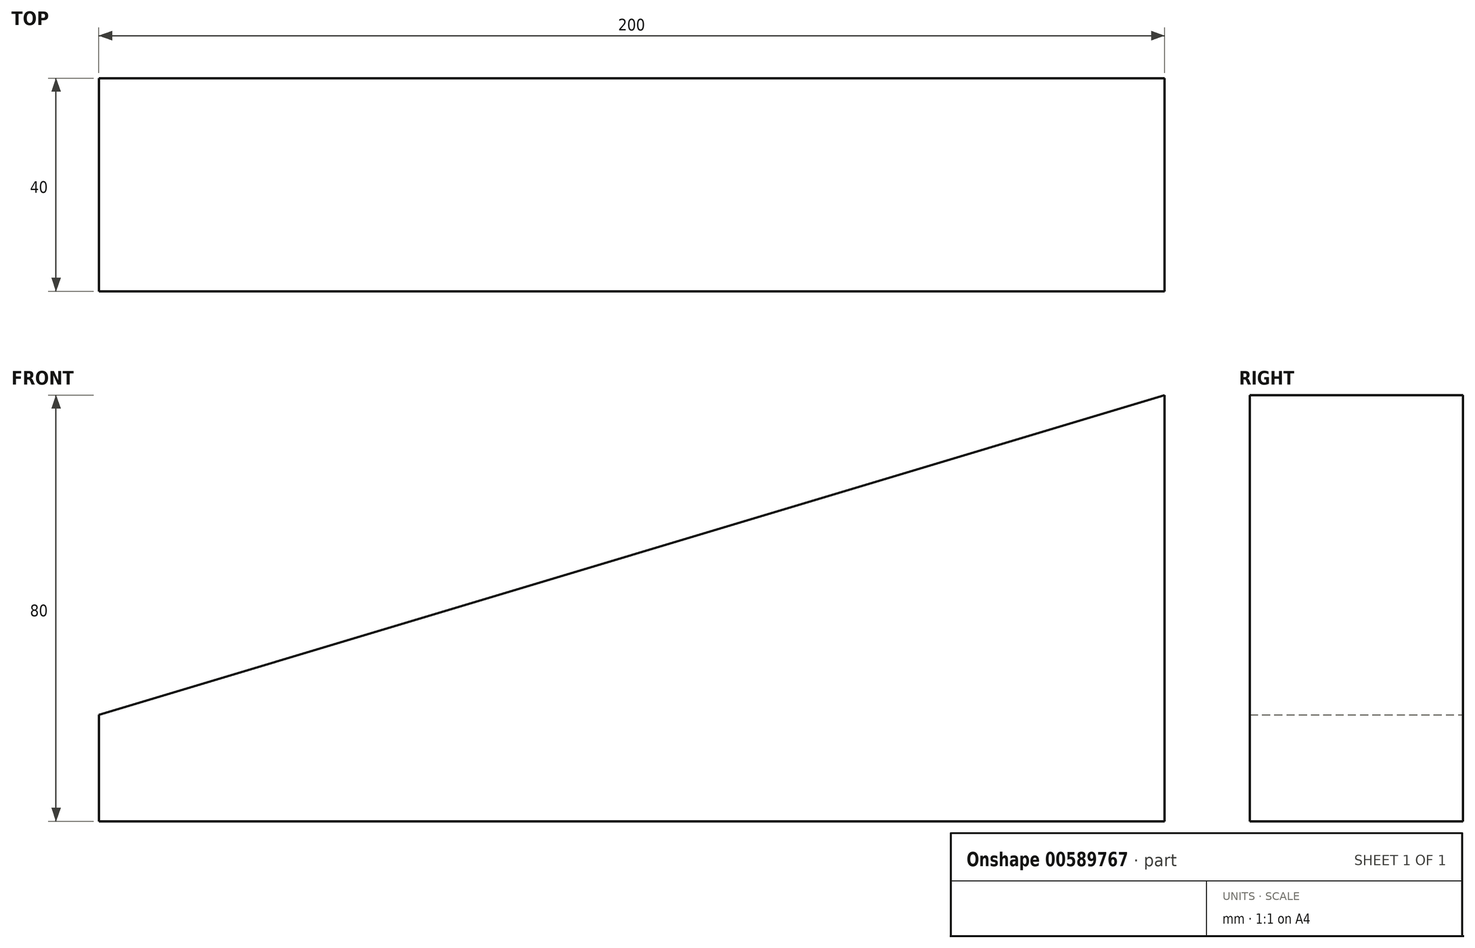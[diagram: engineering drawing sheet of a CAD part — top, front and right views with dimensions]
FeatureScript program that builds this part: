
annotation { "Feature Type Name" : "Feature", "Feature Type Description" : "" }
export const myFeature = defineFeature(function(context is Context, id is Id, definition is map)
    precondition{}
    {
        {
            var Q0;
            Q0=qCreatedBy(makeId("Front.planeOp"),FACE);
            var sketch = newSketch(context, id + "F0", { "sketchPlane" : qUnion([Q0])});
            skLineSegment(sketch, "E0", {"start": v(-96.18, 0) * mm, "end": v(103.82, 0) * mm});
            skLineSegment(sketch, "E1", {"start": v(103.82, 0) * mm, "end": v(103.82, 80) * mm});
            skLineSegment(sketch, "E2", {"start": v(-96.18, 0) * mm, "end": v(-96.18, 20) * mm});
            skLineSegment(sketch, "E3", {"start": v(-96.18, 20) * mm, "end": v(103.82, 80) * mm});
            skSolve(sketch);
        }
        {
            var Q0;
            Q0=makeQuery(id+"F0.imprint","IMPRINT",FACE,{"disambiguationData":[TD([[makeQuery(id+"F0.imprint","IMPRINT",EDGE,{"derivedFrom":sQuery(id+"F0.wireOp",EDGE,"E0")}),1.0]])]});
            extrude(context, id + "F1", {"entities" : qUnion([Q0]), "depth" : 40 * mm, "offsetDistance" : 25 * mm});
        }
    });
